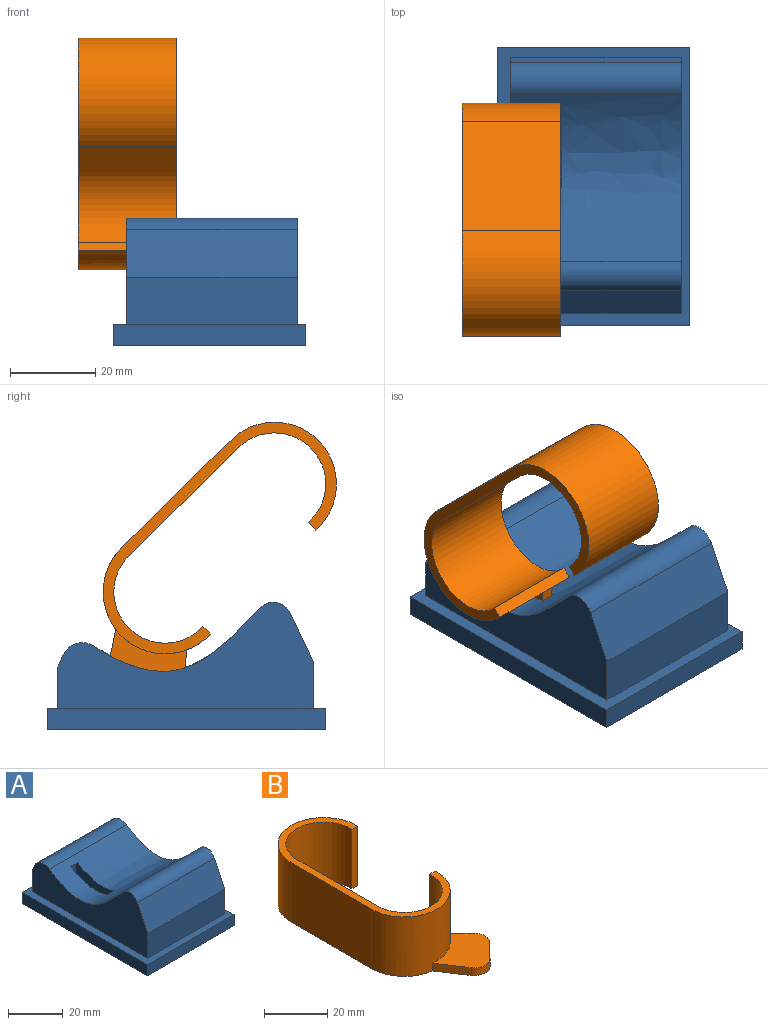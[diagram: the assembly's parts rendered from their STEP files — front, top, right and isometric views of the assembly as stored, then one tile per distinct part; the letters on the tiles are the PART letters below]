
ASSEMBLY  parts=2 mates=1
PART A: 21 faces, bbox 45x65x29.8 mm
  f0: plane 45x5mm, normal (0,-1,0), area 225mm2, adj f1,f3,f4,f5
  f1: plane 65x45mm, normal (0,0,-1), area 2925mm2, adj f0,f2,f4,f5
  f2: plane 45x5mm, normal (0,1,0), area 225mm2, adj f1,f3,f4,f5
  f3: plane 65x45mm, normal (0,0,1), area 525.1mm2, adj f0,f2,f4,f5,f6,f7,f13,f14
  f4: plane 65x5mm, normal (1,0,0), area 325mm2, adj f0,f1,f2,f3
  f5: plane 65x5mm, normal (-1,0,0), area 325mm2, adj f0,f1,f2,f3
  f6: plane 40x11.07mm, normal (0,-1,0), area 442.7mm2, adj f3,f12,f13,f14
  f7: plane 40x9.45mm, normal (0,1,0), area 377.8mm2, adj f3,f8,f13,f14
  f8: plane 40x2.98mm, normal (0,0.91,0.41), area 130.3mm2, adj f7,f9,f13,f14
  f9: cylinder r=5mm len=40mm, axis (-1,0,0), area 354.3mm2, adj f8,f10,f13,f14
  f10: extruded ~40x39.07mm, area 1759.7mm2, adj f9,f11,f13,f14,f15,f18,f19,f20
  f11: cylinder r=4.45mm len=40mm, axis (-1,0,0), area 318.2mm2, adj f10,f12,f13,f14
  f12: plane 40x11.25mm, normal (0,-0.9,0.43), area 499.1mm2, adj f6,f11,f13,f14
  f13: plane 60x24.85mm, normal (1,0,0), area 875mm2, adj f3,f6,f7,f8,f9,f10,f11,f12
  f14: plane 60x24.85mm, normal (-1,0,0), area 875mm2, adj f3,f6,f7,f8,f9,f10,f11,f12
  f15: plane 9.42x3.5mm, normal (0,1,0), area 33mm2, adj f10,f16,f19,f20
  f16: plane 20x3.5mm, normal (0,0,1), area 70mm2, adj f15,f17,f19,f20
  f17: plane 12.51x3.5mm, normal (0,-1,0), area 43.8mm2, adj f16,f18,f19,f20
  f18: plane 3.5x0.94mm, normal (0,0,-1), area 3.3mm2, adj f10,f17,f19,f20
  f19: plane 20.12x12.63mm, normal (-1,0,0), area 193.1mm2, adj f10,f15,f16,f17,f18
  f20: plane 20.12x12.63mm, normal (1,0,0), area 193.1mm2, adj f10,f15,f16,f17,f18
PART B: 16 faces, bbox 35x77.5x23 mm
  f0: plane 36x23mm, normal (-1,0,0), area 828mm2, adj f1,f7,f8,f13
  f1: cylinder r=14.5mm len=29mm, axis (0,0,-1), area 1007.4mm2, adj f0,f2,f8,f9,f10,f11,f13
  f2: plane 23x2.5mm, normal (-0.01,1,0), area 57.5mm2, adj f1,f3,f8,f13
  f3: cylinder r=12mm len=24mm, axis (0,0,-1), area 881.1mm2, adj f2,f4,f8,f13
  f4: plane 36x23mm, normal (1,0,0), area 828mm2, adj f3,f5,f8,f13
  f5: cylinder r=12mm len=24mm, axis (0,0,-1), area 881.1mm2, adj f4,f6,f8,f13
  f6: plane 23x2.5mm, normal (-0.01,-1,0), area 57.5mm2, adj f5,f7,f8,f13
  f7: cylinder r=14.5mm len=29mm, axis (0,0,-1), area 1062.6mm2, adj f0,f6,f8,f13
  f8: plane 65x29mm, normal (0,0,1), area 301.3mm2, adj f0,f1,f2,f3,f4,f5,f6,f7
  f9: plane 22.34x20.98mm, normal (0,0,1), area 246.9mm2, adj f1,f10,f11,f12,f14,f15
  f10: plane 6.13x5.91mm, normal (0.72,0.69,0), area 25.5mm2, adj f1,f9,f13,f15
  f11: plane 10.4x6.88mm, normal (-0.83,-0.55,0), area 37.4mm2, adj f1,f9,f13,f14
  f12: plane 6.38x6.29mm, normal (0.71,-0.7,0), area 26.9mm2, adj f9,f13,f14,f15
  f13: plane 77.52x35mm, normal (0,0,-1), area 548.2mm2, adj f0,f1,f2,f3,f4,f5,f6,f7
  f14: cylinder r=5mm len=7.73mm, axis (0,0,1), area 26.7mm2, adj f9,f11,f12,f13
  f15: cylinder r=5mm len=6.98mm, axis (0,0,1), area 23.2mm2, adj f9,f10,f12,f13
PLACE A t=(-4.8,-33.37,-29.36)mm
PLACE B rot(axis=(0.68,-0.28,-0.68),148.9deg) t=(6.85,-0.29,24.11)mm
MATE fastened B.f12 <-> A.f16  axis (0,0,-1) through (8.35,8.85,-24.09)mm
